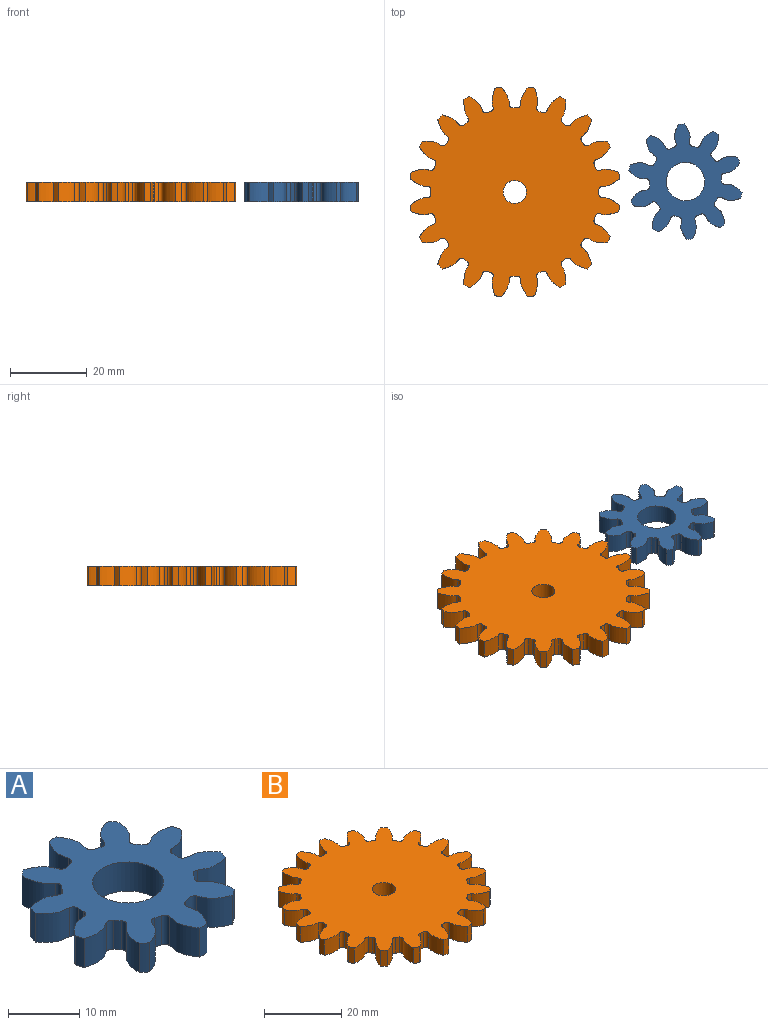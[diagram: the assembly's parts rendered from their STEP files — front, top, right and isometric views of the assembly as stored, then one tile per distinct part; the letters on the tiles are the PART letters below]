
ASSEMBLY  parts=2 mates=1
PART A: 63 faces, bbox 29x30.1x5 mm
  f0: extruded ~5x4.35mm, area 25.9mm2, adj f39,f40,f41,f42
  f1: cylinder r=9.38mm len=5mm, axis (0,0,-1), area 5.2mm2, adj f40,f41,f42,f43
  f2: extruded ~5x4.35mm, area 25.9mm2, adj f3,f40,f41,f43
  f3: cylinder r=15mm len=5mm, axis (0,0,-1), area 7.3mm2, adj f2,f4,f40,f41
  f4: extruded ~5x4.98mm, area 25.9mm2, adj f3,f40,f41,f44
  f5: cylinder r=9.38mm len=5mm, axis (0,0,-1), area 5.2mm2, adj f40,f41,f44,f45
  f6: extruded ~5x4.57mm, area 25.9mm2, adj f7,f40,f41,f45
  f7: cylinder r=15mm len=5mm, axis (0,0,-1), area 7.3mm2, adj f6,f8,f40,f41
  f8: extruded ~5x3.71mm, area 25.9mm2, adj f7,f40,f41,f46
  f9: cylinder r=9.38mm len=5mm, axis (0,0,-1), area 5.2mm2, adj f40,f41,f46,f47
  f10: extruded ~5x4.91mm, area 25.9mm2, adj f11,f40,f41,f47
  f11: cylinder r=15mm len=5mm, axis (0,0,-1), area 7.3mm2, adj f10,f12,f40,f41
  f12: extruded ~5x4.91mm, area 25.9mm2, adj f11,f40,f41,f48
  f13: cylinder r=9.38mm len=5mm, axis (0,0,-1), area 5.2mm2, adj f40,f41,f48,f49
  f14: extruded ~5x3.71mm, area 25.9mm2, adj f15,f40,f41,f49
  f15: cylinder r=15mm len=5mm, axis (0,0,-1), area 7.3mm2, adj f14,f16,f40,f41
  f16: extruded ~5x4.57mm, area 25.9mm2, adj f15,f40,f41,f50
  f17: cylinder r=9.38mm len=5mm, axis (0,0,-1), area 5.2mm2, adj f40,f41,f50,f51
  f18: extruded ~5x4.98mm, area 25.9mm2, adj f19,f40,f41,f51
  f19: cylinder r=15mm len=5mm, axis (0,0,-1), area 7.3mm2, adj f18,f20,f40,f41
  f20: extruded ~5x4.35mm, area 25.9mm2, adj f19,f40,f41,f52
  f21: cylinder r=9.38mm len=5mm, axis (0,0,-1), area 5.2mm2, adj f40,f41,f52,f53
  f22: extruded ~5x4.35mm, area 25.9mm2, adj f23,f40,f41,f53
  f23: cylinder r=15mm len=5mm, axis (0,0,-1), area 7.3mm2, adj f22,f24,f40,f41
  f24: extruded ~5x4.98mm, area 25.9mm2, adj f23,f40,f41,f54
  f25: cylinder r=9.38mm len=5mm, axis (0,0,-1), area 5.2mm2, adj f40,f41,f54,f55
  f26: extruded ~5x4.57mm, area 25.9mm2, adj f27,f40,f41,f55
  f27: cylinder r=15mm len=5mm, axis (0,0,-1), area 7.3mm2, adj f26,f28,f40,f41
  f28: extruded ~5x3.71mm, area 25.9mm2, adj f27,f40,f41,f56
  f29: cylinder r=9.38mm len=5mm, axis (0,0,-1), area 5.2mm2, adj f40,f41,f56,f57
  f30: extruded ~5x4.91mm, area 25.9mm2, adj f31,f40,f41,f57
  f31: cylinder r=15mm len=5mm, axis (0,0,-1), area 7.3mm2, adj f30,f32,f40,f41
  f32: extruded ~5x4.91mm, area 25.9mm2, adj f31,f40,f41,f58
  f33: cylinder r=9.38mm len=5mm, axis (0,0,-1), area 5.2mm2, adj f40,f41,f58,f59
  f34: extruded ~5x3.71mm, area 25.9mm2, adj f35,f40,f41,f59
  f35: cylinder r=15mm len=5mm, axis (0,0,-1), area 7.3mm2, adj f34,f36,f40,f41
  f36: extruded ~5x4.57mm, area 25.9mm2, adj f35,f40,f41,f60
  f37: cylinder r=9.38mm len=5mm, axis (0,0,-1), area 5.2mm2, adj f40,f41,f60,f61
  f38: extruded ~5x4.98mm, area 25.9mm2, adj f39,f40,f41,f61
  f39: cylinder r=15mm len=5mm, axis (0,0,-1), area 7.3mm2, adj f0,f38,f40,f41
  f40: plane 30.05x29.02mm, normal (0,0,1), area 390mm2, adj f0,f1,f2,f3,f4,f5,f6,f7
  f41: plane 30.05x29.02mm, normal (0,0,-1), area 390mm2, adj f0,f1,f2,f3,f4,f5,f6,f7
  f42: cylinder r=0.89mm len=5mm, axis (0,0,-1), area 6.6mm2, adj f0,f1,f40,f41
  f43: cylinder r=0.89mm len=5mm, axis (0,0,-1), area 6.6mm2, adj f1,f2,f40,f41
  f44: cylinder r=0.89mm len=5mm, axis (0,0,-1), area 6.6mm2, adj f4,f5,f40,f41
  f45: cylinder r=0.89mm len=5mm, axis (0,0,-1), area 6.6mm2, adj f5,f6,f40,f41
  f46: cylinder r=0.89mm len=5mm, axis (0,0,-1), area 6.6mm2, adj f8,f9,f40,f41
  f47: cylinder r=0.89mm len=5mm, axis (0,0,-1), area 6.6mm2, adj f9,f10,f40,f41
  f48: cylinder r=0.89mm len=5mm, axis (0,0,-1), area 6.6mm2, adj f12,f13,f40,f41
  f49: cylinder r=0.89mm len=5mm, axis (0,0,-1), area 6.6mm2, adj f13,f14,f40,f41
  f50: cylinder r=0.89mm len=5mm, axis (0,0,-1), area 6.6mm2, adj f16,f17,f40,f41
  f51: cylinder r=0.89mm len=5mm, axis (0,0,-1), area 6.6mm2, adj f17,f18,f40,f41
  f52: cylinder r=0.89mm len=5mm, axis (0,0,-1), area 6.6mm2, adj f20,f21,f40,f41
  f53: cylinder r=0.89mm len=5mm, axis (0,0,-1), area 6.6mm2, adj f21,f22,f40,f41
  f54: cylinder r=0.89mm len=5mm, axis (0,0,-1), area 6.6mm2, adj f24,f25,f40,f41
  f55: cylinder r=0.89mm len=5mm, axis (0,0,-1), area 6.6mm2, adj f25,f26,f40,f41
  f56: cylinder r=0.89mm len=5mm, axis (0,0,-1), area 6.6mm2, adj f28,f29,f40,f41
  f57: cylinder r=0.89mm len=5mm, axis (0,0,-1), area 6.6mm2, adj f29,f30,f40,f41
  f58: cylinder r=0.89mm len=5mm, axis (0,0,-1), area 6.6mm2, adj f32,f33,f40,f41
  f59: cylinder r=0.89mm len=5mm, axis (0,0,-1), area 6.6mm2, adj f33,f34,f40,f41
  f60: cylinder r=0.89mm len=5mm, axis (0,0,-1), area 6.6mm2, adj f36,f37,f40,f41
  f61: cylinder r=0.89mm len=5mm, axis (0,0,-1), area 6.6mm2, adj f37,f38,f40,f41
  f62: cylinder r=5mm len=10mm, axis (0,0,-1), area 157.1mm2, adj f40,f41
PART B: 123 faces, bbox 54.6x54.6x5 mm
  f0: extruded ~5x4.54mm, area 25.3mm2, adj f79,f80,f81,f82
  f1: cylinder r=21.88mm len=5mm, axis (0,0,-1), area 5mm2, adj f80,f81,f82,f83
  f2: extruded ~5x4.54mm, area 25.3mm2, adj f3,f80,f81,f83
  f3: cylinder r=27.5mm len=5mm, axis (0,0,-1), area 8.7mm2, adj f2,f4,f80,f81
  f4: extruded ~5x4.94mm, area 25.3mm2, adj f3,f80,f81,f84
  f5: cylinder r=21.88mm len=5mm, axis (0,0,-1), area 5mm2, adj f80,f81,f84,f85
  f6: extruded ~5x3.71mm, area 25.3mm2, adj f7,f80,f81,f85
  f7: cylinder r=27.5mm len=5mm, axis (0,0,-1), area 8.7mm2, adj f6,f8,f80,f81
  f8: extruded ~5x4.85mm, area 25.3mm2, adj f7,f80,f81,f86
  f9: cylinder r=21.88mm len=5mm, axis (0,0,-1), area 5mm2, adj f80,f81,f86,f87
  f10: extruded ~5x4.29mm, area 25.3mm2, adj f11,f80,f81,f87
  f11: cylinder r=27.5mm len=5mm, axis (0,0,-1), area 8.7mm2, adj f10,f12,f80,f81
  f12: extruded ~5x4.29mm, area 25.3mm2, adj f11,f80,f81,f88
  f13: cylinder r=21.88mm len=5mm, axis (0,0,-1), area 5mm2, adj f80,f81,f88,f89
  f14: extruded ~5x4.85mm, area 25.3mm2, adj f15,f80,f81,f89
  f15: cylinder r=27.5mm len=5mm, axis (0,0,-1), area 8.7mm2, adj f14,f16,f80,f81
  f16: extruded ~5x3.71mm, area 25.3mm2, adj f15,f80,f81,f90
  f17: cylinder r=21.88mm len=5mm, axis (0,0,-1), area 5mm2, adj f80,f81,f90,f91
  f18: extruded ~5x4.94mm, area 25.3mm2, adj f19,f80,f81,f91
  f19: cylinder r=27.5mm len=5mm, axis (0,0,-1), area 8.7mm2, adj f18,f20,f80,f81
  f20: extruded ~5x4.54mm, area 25.3mm2, adj f19,f80,f81,f92
  f21: cylinder r=21.88mm len=5mm, axis (0,0,-1), area 5mm2, adj f80,f81,f92,f93
  f22: extruded ~5x4.54mm, area 25.3mm2, adj f23,f80,f81,f93
  f23: cylinder r=27.5mm len=5mm, axis (0,0,-1), area 8.7mm2, adj f22,f24,f80,f81
  f24: extruded ~5x4.94mm, area 25.3mm2, adj f23,f80,f81,f94
  f25: cylinder r=21.88mm len=5mm, axis (0,0,-1), area 5mm2, adj f80,f81,f94,f95
  f26: extruded ~5x3.71mm, area 25.3mm2, adj f27,f80,f81,f95
  f27: cylinder r=27.5mm len=5mm, axis (0,0,-1), area 8.7mm2, adj f26,f28,f80,f81
  f28: extruded ~5x4.85mm, area 25.3mm2, adj f27,f80,f81,f96
  f29: cylinder r=21.88mm len=5mm, axis (0,0,-1), area 5mm2, adj f80,f81,f96,f97
  f30: extruded ~5x4.29mm, area 25.3mm2, adj f31,f80,f81,f97
  f31: cylinder r=27.5mm len=5mm, axis (0,0,-1), area 8.7mm2, adj f30,f32,f80,f81
  f32: extruded ~5x4.29mm, area 25.3mm2, adj f31,f80,f81,f98
  f33: cylinder r=21.88mm len=5mm, axis (0,0,-1), area 5mm2, adj f80,f81,f98,f99
  f34: extruded ~5x4.85mm, area 25.3mm2, adj f35,f80,f81,f99
  f35: cylinder r=27.5mm len=5mm, axis (0,0,-1), area 8.7mm2, adj f34,f36,f80,f81
  f36: extruded ~5x3.71mm, area 25.3mm2, adj f35,f80,f81,f100
  f37: cylinder r=21.88mm len=5mm, axis (0,0,-1), area 5mm2, adj f80,f81,f100,f101
  f38: extruded ~5x4.94mm, area 25.3mm2, adj f39,f80,f81,f101
  f39: cylinder r=27.5mm len=5mm, axis (0,0,-1), area 8.7mm2, adj f38,f40,f80,f81
  f40: extruded ~5x4.54mm, area 25.3mm2, adj f39,f80,f81,f102
  f41: cylinder r=21.88mm len=5mm, axis (0,0,-1), area 5mm2, adj f80,f81,f102,f103
  f42: extruded ~5x4.54mm, area 25.3mm2, adj f43,f80,f81,f103
  f43: cylinder r=27.5mm len=5mm, axis (0,0,-1), area 8.7mm2, adj f42,f44,f80,f81
  f44: extruded ~5x4.94mm, area 25.3mm2, adj f43,f80,f81,f104
  f45: cylinder r=21.88mm len=5mm, axis (0,0,-1), area 5mm2, adj f80,f81,f104,f105
  f46: extruded ~5x3.71mm, area 25.3mm2, adj f47,f80,f81,f105
  f47: cylinder r=27.5mm len=5mm, axis (0,0,-1), area 8.7mm2, adj f46,f48,f80,f81
  f48: extruded ~5x4.85mm, area 25.3mm2, adj f47,f80,f81,f106
  f49: cylinder r=21.88mm len=5mm, axis (0,0,-1), area 5mm2, adj f80,f81,f106,f107
  f50: extruded ~5x4.29mm, area 25.3mm2, adj f51,f80,f81,f107
  f51: cylinder r=27.5mm len=5mm, axis (0,0,-1), area 8.7mm2, adj f50,f52,f80,f81
  f52: extruded ~5x4.29mm, area 25.3mm2, adj f51,f80,f81,f108
  f53: cylinder r=21.88mm len=5mm, axis (0,0,-1), area 5mm2, adj f80,f81,f108,f109
  f54: extruded ~5x4.85mm, area 25.3mm2, adj f55,f80,f81,f109
  f55: cylinder r=27.5mm len=5mm, axis (0,0,-1), area 8.7mm2, adj f54,f56,f80,f81
  f56: extruded ~5x3.71mm, area 25.3mm2, adj f55,f80,f81,f110
  f57: cylinder r=21.88mm len=5mm, axis (0,0,-1), area 5mm2, adj f80,f81,f110,f111
  f58: extruded ~5x4.94mm, area 25.3mm2, adj f59,f80,f81,f111
  f59: cylinder r=27.5mm len=5mm, axis (0,0,-1), area 8.7mm2, adj f58,f60,f80,f81
  f60: extruded ~5x4.54mm, area 25.3mm2, adj f59,f80,f81,f112
  f61: cylinder r=21.88mm len=5mm, axis (0,0,-1), area 5mm2, adj f80,f81,f112,f113
  f62: extruded ~5x4.54mm, area 25.3mm2, adj f63,f80,f81,f113
  f63: cylinder r=27.5mm len=5mm, axis (0,0,-1), area 8.7mm2, adj f62,f64,f80,f81
  f64: extruded ~5x4.94mm, area 25.3mm2, adj f63,f80,f81,f114
  f65: cylinder r=21.88mm len=5mm, axis (0,0,-1), area 5mm2, adj f80,f81,f114,f115
  f66: extruded ~5x3.71mm, area 25.3mm2, adj f67,f80,f81,f115
  f67: cylinder r=27.5mm len=5mm, axis (0,0,-1), area 8.7mm2, adj f66,f68,f80,f81
  f68: extruded ~5x4.85mm, area 25.3mm2, adj f67,f80,f81,f116
  f69: cylinder r=21.88mm len=5mm, axis (0,0,-1), area 5mm2, adj f80,f81,f116,f117
  f70: extruded ~5x4.29mm, area 25.3mm2, adj f71,f80,f81,f117
  f71: cylinder r=27.5mm len=5mm, axis (0,0,-1), area 8.7mm2, adj f70,f72,f80,f81
  f72: extruded ~5x4.29mm, area 25.3mm2, adj f71,f80,f81,f118
  f73: cylinder r=21.88mm len=5mm, axis (0,0,-1), area 5mm2, adj f80,f81,f118,f119
  f74: extruded ~5x4.85mm, area 25.3mm2, adj f75,f80,f81,f119
  f75: cylinder r=27.5mm len=5mm, axis (0,0,-1), area 8.7mm2, adj f74,f76,f80,f81
  f76: extruded ~5x3.71mm, area 25.3mm2, adj f75,f80,f81,f120
  f77: cylinder r=21.88mm len=5mm, axis (0,0,-1), area 5mm2, adj f80,f81,f120,f121
  f78: extruded ~5x4.94mm, area 25.3mm2, adj f79,f80,f81,f121
  f79: cylinder r=27.5mm len=5mm, axis (0,0,-1), area 8.7mm2, adj f0,f78,f80,f81
  f80: plane 54.61x54.61mm, normal (0,0,1), area 1894.6mm2, adj f0,f1,f2,f3,f4,f5,f6,f7
  f81: plane 54.61x54.61mm, normal (0,0,-1), area 1894.6mm2, adj f0,f1,f2,f3,f4,f5,f6,f7
  f82: cylinder r=0.93mm len=5mm, axis (0,0,-1), area 7.1mm2, adj f0,f1,f80,f81
  f83: cylinder r=0.93mm len=5mm, axis (0,0,-1), area 7.1mm2, adj f1,f2,f80,f81
  f84: cylinder r=0.93mm len=5mm, axis (0,0,-1), area 7.1mm2, adj f4,f5,f80,f81
  f85: cylinder r=0.93mm len=5mm, axis (0,0,-1), area 7.1mm2, adj f5,f6,f80,f81
  f86: cylinder r=0.93mm len=5mm, axis (0,0,-1), area 7.1mm2, adj f8,f9,f80,f81
  f87: cylinder r=0.93mm len=5mm, axis (0,0,-1), area 7.1mm2, adj f9,f10,f80,f81
  f88: cylinder r=0.93mm len=5mm, axis (0,0,-1), area 7.1mm2, adj f12,f13,f80,f81
  f89: cylinder r=0.93mm len=5mm, axis (0,0,-1), area 7.1mm2, adj f13,f14,f80,f81
  f90: cylinder r=0.93mm len=5mm, axis (0,0,-1), area 7.1mm2, adj f16,f17,f80,f81
  f91: cylinder r=0.93mm len=5mm, axis (0,0,-1), area 7.1mm2, adj f17,f18,f80,f81
  f92: cylinder r=0.93mm len=5mm, axis (0,0,-1), area 7.1mm2, adj f20,f21,f80,f81
  f93: cylinder r=0.93mm len=5mm, axis (0,0,-1), area 7.1mm2, adj f21,f22,f80,f81
  f94: cylinder r=0.93mm len=5mm, axis (0,0,-1), area 7.1mm2, adj f24,f25,f80,f81
  f95: cylinder r=0.93mm len=5mm, axis (0,0,-1), area 7.1mm2, adj f25,f26,f80,f81
  f96: cylinder r=0.93mm len=5mm, axis (0,0,-1), area 7.1mm2, adj f28,f29,f80,f81
  f97: cylinder r=0.93mm len=5mm, axis (0,0,-1), area 7.1mm2, adj f29,f30,f80,f81
  f98: cylinder r=0.93mm len=5mm, axis (0,0,-1), area 7.1mm2, adj f32,f33,f80,f81
  f99: cylinder r=0.93mm len=5mm, axis (0,0,-1), area 7.1mm2, adj f33,f34,f80,f81
  f100: cylinder r=0.93mm len=5mm, axis (0,0,-1), area 7.1mm2, adj f36,f37,f80,f81
  f101: cylinder r=0.93mm len=5mm, axis (0,0,-1), area 7.1mm2, adj f37,f38,f80,f81
  f102: cylinder r=0.93mm len=5mm, axis (0,0,-1), area 7.1mm2, adj f40,f41,f80,f81
  f103: cylinder r=0.93mm len=5mm, axis (0,0,-1), area 7.1mm2, adj f41,f42,f80,f81
  f104: cylinder r=0.93mm len=5mm, axis (0,0,-1), area 7.1mm2, adj f44,f45,f80,f81
  f105: cylinder r=0.93mm len=5mm, axis (0,0,-1), area 7.1mm2, adj f45,f46,f80,f81
  f106: cylinder r=0.93mm len=5mm, axis (0,0,-1), area 7.1mm2, adj f48,f49,f80,f81
  f107: cylinder r=0.93mm len=5mm, axis (0,0,-1), area 7.1mm2, adj f49,f50,f80,f81
  f108: cylinder r=0.93mm len=5mm, axis (0,0,-1), area 7.1mm2, adj f52,f53,f80,f81
  f109: cylinder r=0.93mm len=5mm, axis (0,0,-1), area 7.1mm2, adj f53,f54,f80,f81
  f110: cylinder r=0.93mm len=5mm, axis (0,0,-1), area 7.1mm2, adj f56,f57,f80,f81
  f111: cylinder r=0.93mm len=5mm, axis (0,0,-1), area 7.1mm2, adj f57,f58,f80,f81
  f112: cylinder r=0.93mm len=5mm, axis (0,0,-1), area 7.1mm2, adj f60,f61,f80,f81
  f113: cylinder r=0.93mm len=5mm, axis (0,0,-1), area 7.1mm2, adj f61,f62,f80,f81
  f114: cylinder r=0.93mm len=5mm, axis (0,0,-1), area 7.1mm2, adj f64,f65,f80,f81
  f115: cylinder r=0.93mm len=5mm, axis (0,0,-1), area 7.1mm2, adj f65,f66,f80,f81
  f116: cylinder r=0.93mm len=5mm, axis (0,0,-1), area 7.1mm2, adj f68,f69,f80,f81
  f117: cylinder r=0.93mm len=5mm, axis (0,0,-1), area 7.1mm2, adj f69,f70,f80,f81
  f118: cylinder r=0.93mm len=5mm, axis (0,0,-1), area 7.1mm2, adj f72,f73,f80,f81
  f119: cylinder r=0.93mm len=5mm, axis (0,0,-1), area 7.1mm2, adj f73,f74,f80,f81
  f120: cylinder r=0.93mm len=5mm, axis (0,0,-1), area 7.1mm2, adj f76,f77,f80,f81
  f121: cylinder r=0.93mm len=5mm, axis (0,0,-1), area 7.1mm2, adj f77,f78,f80,f81
  f122: cylinder r=3mm len=6mm, axis (0,0,1), area 94.2mm2, adj f80,f81
PLACE A rot(axis=(0,0,1),40deg) t=(23.47,-20,3.55)mm
PLACE B t=(-43.43,-22.7,3.55)mm fixed
MATE planar A.f1 <-> B.f65  axis (0,0,1) through (23.47,-20,8.55)mm
